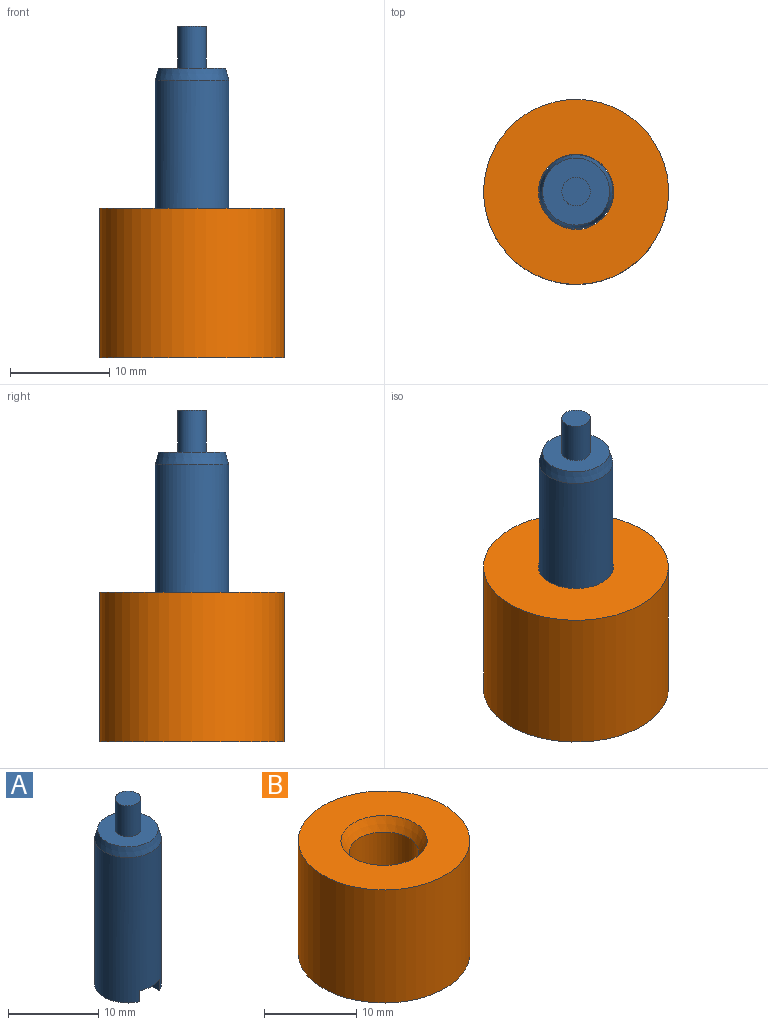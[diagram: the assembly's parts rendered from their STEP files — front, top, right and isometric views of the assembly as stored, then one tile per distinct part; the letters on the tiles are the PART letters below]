
ASSEMBLY  parts=2 mates=1
PART A: 10 faces, bbox 7.4x7.4x25.2 mm
  f0: plane 6.75x2.2mm, normal (0,0,-1), area 10.7mm2, adj f1,f5
  f1: plane 6.75x1.5mm, normal (-1,0,0), area 10.1mm2, adj f0,f2,f5
  f2: plane 7.39x3mm, normal (0,0,-1), area 21.5mm2, adj f1,f3,f5
  f3: plane 6.75x1.5mm, normal (1,0,0), area 10.1mm2, adj f2,f4,f5
  f4: plane 6.75x2.2mm, normal (0,0,-1), area 10.7mm2, adj f3,f5
  f5: cylinder r=3.69mm len=19.77mm, axis (0,0,-1), area 449.7mm2, adj f0,f1,f2,f3,f4,f8
  f6: plane 6.73x6.73mm, normal (0,0,1), area 29.1mm2, adj f7,f8
  f7: cylinder r=1.44mm len=4.2mm, axis (0,0,-1), area 37.9mm2, adj f6,f9
  f8: cone r=3.36mm half-angle=15deg, axis (0,0,-1), area 28.3mm2, adj f5,f6
  f9: plane 2.88x2.88mm, normal (0,0,1), area 6.5mm2, adj f7
PART B: 5 faces, bbox 18.6x18.6x15 mm
  f0: cylinder r=3.78mm len=13.44mm, axis (0,0,-1), area 319.2mm2, adj f3,f4
  f1: cylinder r=9.3mm len=18.6mm, axis (0,0,-1), area 876.5mm2, adj f2,f3
  f2: plane 18.6x18.6mm, normal (0,0,1), area 202.9mm2, adj f1,f4
  f3: plane 18.6x18.6mm, normal (0,0,-1), area 226.8mm2, adj f0,f1
  f4: cone r=3.78mm half-angle=30deg, axis (0,0,1), area 47.8mm2, adj f0,f2
PLACE A at identity
PLACE B rot(axis=(0,1,0),180deg) t=(0,0,91.5)mm fixed
MATE fastened A.f5 <-> B.f0  axis (0,0,1) through (0,0,105.6)mm
